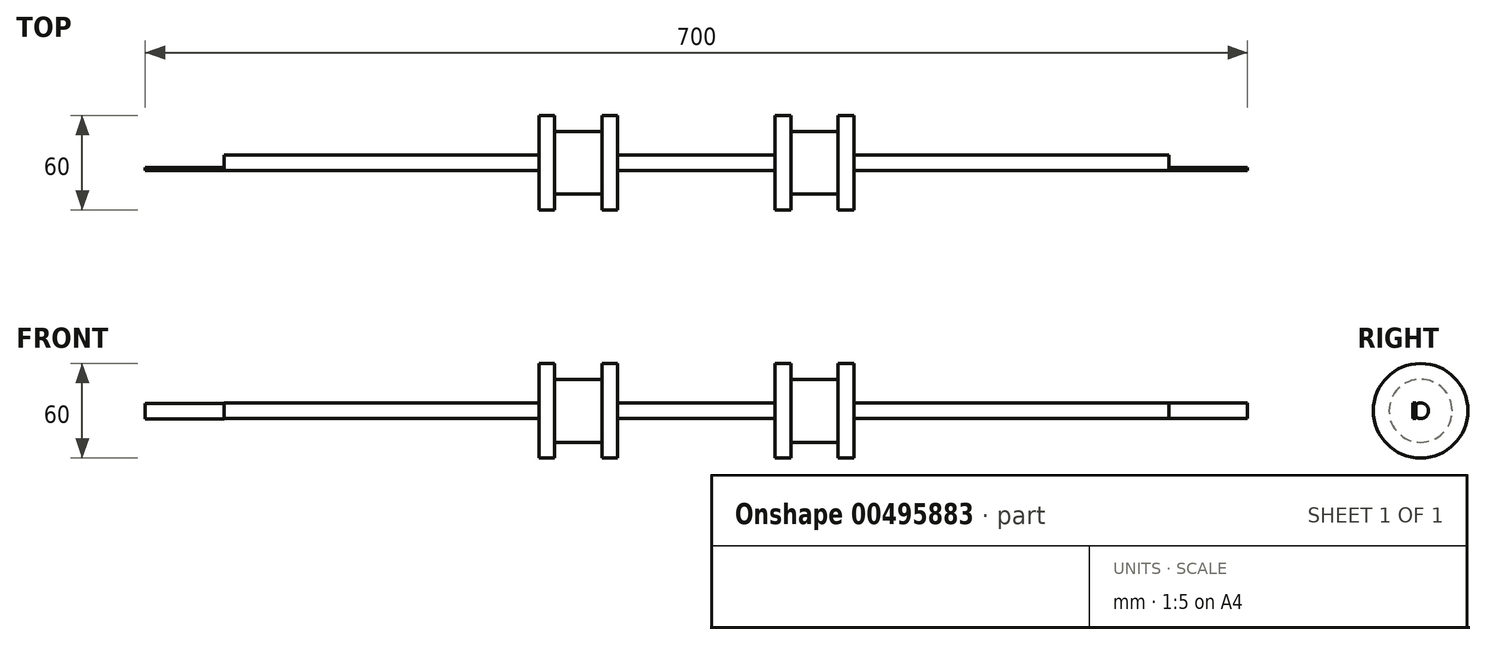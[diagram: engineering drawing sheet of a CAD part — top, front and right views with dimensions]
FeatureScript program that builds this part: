
annotation { "Feature Type Name" : "Feature", "Feature Type Description" : "" }
export const myFeature = defineFeature(function(context is Context, id is Id, definition is map)
    precondition{}
    {
        {
            var Q0;
            Q0=qCreatedBy(makeId("Top.planeOp"),FACE);
            var sketch = newSketch(context, id + "F0", { "sketchPlane" : qUnion([Q0])});
            skLineSegment(sketch, "E0", {"start": v(-300, 0) * mm, "end": v(300, 0) * mm});
            skLineSegment(sketch, "E1", {"start": v(-300, 0) * mm, "end": v(-300, 5) * mm});
            skLineSegment(sketch, "E2", {"start": v(-300, 5) * mm, "end": v(300, 5) * mm});
            skLineSegment(sketch, "E3", {"start": v(300, 5) * mm, "end": v(300, 0) * mm});
            skLineSegment(sketch, "E4", {"start": v(-100, 0) * mm, "end": v(-100, -25) * mm});
            skLineSegment(sketch, "E5", {"start": v(-100, -25) * mm, "end": v(-90, -25) * mm});
            skLineSegment(sketch, "E6", {"start": v(-90, -25) * mm, "end": v(-90, -15) * mm});
            skLineSegment(sketch, "E7", {"start": v(-90, -15) * mm, "end": v(-60, -15) * mm});
            skLineSegment(sketch, "E8", {"start": v(-60, -15) * mm, "end": v(-60, -25) * mm});
            skLineSegment(sketch, "E9", {"start": v(-60, -25) * mm, "end": v(-50, -25) * mm});
            skLineSegment(sketch, "E10", {"start": v(-50, -25) * mm, "end": v(-50, 0) * mm});
            skLineSegment(sketch, "E11", {"start": v(50, 0) * mm, "end": v(50, -25) * mm});
            skLineSegment(sketch, "E12", {"start": v(50, -25) * mm, "end": v(60, -25) * mm});
            skLineSegment(sketch, "E13", {"start": v(60, -25) * mm, "end": v(60, -15) * mm});
            skLineSegment(sketch, "E14", {"start": v(60, -15) * mm, "end": v(90, -15) * mm});
            skLineSegment(sketch, "E15", {"start": v(90, -15) * mm, "end": v(90, -25) * mm});
            skLineSegment(sketch, "E16", {"start": v(90, -25) * mm, "end": v(100, -25) * mm});
            skLineSegment(sketch, "E17", {"start": v(100, -25) * mm, "end": v(100, 0) * mm});
            skSolve(sketch);
        }
        {
            var Q0;
            {var subQ5=sQuery(id+"F0.wireOp",EDGE,"E1");Q0=makeQuery(id+"F0.imprint","IMPRINT",FACE,{"disambiguationData":[TD([[makeQuery(id+"F0.imprint","IMPRINT",EDGE,{"derivedFrom":subQ5}),-1.0]])]});}
            var Q1;
            {var subQ0=sQuery(id+"F0.wireOp",EDGE,"E4");Q1=makeQuery(id+"F0.imprint","IMPRINT",FACE,{"disambiguationData":[TD([[makeQuery(id+"F0.imprint","IMPRINT",EDGE,{"derivedFrom":subQ0}),1.0]])]});}
            var Q2;
            {var subQ0=sQuery(id+"F0.wireOp",EDGE,"E11");Q2=makeQuery(id+"F0.imprint","IMPRINT",FACE,{"disambiguationData":[TD([[makeQuery(id+"F0.imprint","IMPRINT",EDGE,{"derivedFrom":subQ0}),1.0]])]});}
            var Q3;
            Q3=sQuery(id+"F0.wireOp",EDGE,"E2");
            revolve(context, id + "F1", {"entities" : qUnion([Q0, Q1, Q2]), "axis" : qUnion([Q3]), "revolveType" : RevolveType.FULL});
        }
        {
            var Q0;
            Q0=makeQuery(id+"F1.opRevolve","SWEPT_FACE",FACE,{"disambiguationData":[OSD([sQuery(id+"F0.wireOp",EDGE,"E1")])]});
            var sketch = newSketch(context, id + "F2", { "sketchPlane" : qUnion([Q0])});
            skLineSegment(sketch, "E18.bottom", {"start": v(-2, 4.74) * mm, "end": v(0, 4.74) * mm});
            skLineSegment(sketch, "E18.top", {"start": v(-2, -5.26) * mm, "end": v(0, -5.26) * mm});
            skLineSegment(sketch, "E18.left", {"start": v(-2, 4.74) * mm, "end": v(-2, -5.26) * mm});
            skLineSegment(sketch, "E18.right", {"start": v(0, 4.74) * mm, "end": v(0, -5.26) * mm});
            skSolve(sketch);
        }
        {
            var Q0;
            {var subQ0=sQuery(id+"F2.wireOp",EDGE,"E18.top");Q0=makeQuery(id+"F2.imprint","IMPRINT",FACE,{"disambiguationData":[TD([[makeQuery(id+"F2.imprint","IMPRINT",EDGE,{"derivedFrom":subQ0}),1.0]])]});}
            var Q1;
            {var subQ0=sQuery(id+"F2.wireOp",EDGE,"E18.left");var subQ1=makeQuery(id+"F1.opRevolve","SWEPT_EDGE",EDGE,{"disambiguationData":[OSD([sQuery(id+"F0.wireOp",EDGE,"E0"),sQuery(id+"F0.wireOp",EDGE,"E1")])]});var subQ2=makeQuery(id+"F2.imprint","INTERSECT",VERTEX,{"disambiguationData":[OD(0.0)],"derivedFrom":[subQ1,subQ0]});Q1=makeQuery(id+"F2.imprint","IMPRINT",FACE,{"disambiguationData":[TD([[makeQuery(id+"F2.imprint","IMPRINT",EDGE,{"disambiguationData":[TD([[subQ2,-1.0]])],"derivedFrom":subQ0}),1.0]])]});}
            var Q2;
            {var subQ0=sQuery(id+"F2.wireOp",EDGE,"E18.bottom");Q2=makeQuery(id+"F2.imprint","IMPRINT",FACE,{"disambiguationData":[TD([[makeQuery(id+"F2.imprint","IMPRINT",EDGE,{"derivedFrom":subQ0}),-1.0]])]});}
            extrude(context, id + "F3", {"entities" : qUnion([Q0, Q1, Q2]), "operationType" : NewBodyOperationType.ADD, "depth" : 50 * mm});
        }
        {
            var Q0;
            Q0=makeQuery(id+"F1.opRevolve","SWEPT_FACE",FACE,{"disambiguationData":[OSD([sQuery(id+"F0.wireOp",EDGE,"E3")])]});
            var sketch = newSketch(context, id + "F4", { "sketchPlane" : qUnion([Q0])});
            skLineSegment(sketch, "E19.bottom", {"start": v(0, 5) * mm, "end": v(2, 5) * mm});
            skLineSegment(sketch, "E19.top", {"start": v(0, -5) * mm, "end": v(2, -5) * mm});
            skLineSegment(sketch, "E19.left", {"start": v(0, 5) * mm, "end": v(0, -5) * mm});
            skLineSegment(sketch, "E19.right", {"start": v(2, 5) * mm, "end": v(2, -5) * mm});
            skSolve(sketch);
        }
        {
            var Q0;
            {var subQ0=sQuery(id+"F4.wireOp",EDGE,"E19.top");Q0=makeQuery(id+"F4.imprint","IMPRINT",FACE,{"disambiguationData":[TD([[makeQuery(id+"F4.imprint","IMPRINT",EDGE,{"derivedFrom":subQ0}),1.0]])]});}
            var Q1;
            {var subQ0=sQuery(id+"F4.wireOp",EDGE,"E19.bottom");Q1=makeQuery(id+"F4.imprint","IMPRINT",FACE,{"disambiguationData":[TD([[makeQuery(id+"F4.imprint","IMPRINT",EDGE,{"derivedFrom":subQ0}),-1.0]])]});}
            var Q2;
            {var subQ0=sQuery(id+"F4.wireOp",EDGE,"E19.right");var subQ1=makeQuery(id+"F1.opRevolve","SWEPT_EDGE",EDGE,{"disambiguationData":[OSD([sQuery(id+"F0.wireOp",EDGE,"E0"),sQuery(id+"F0.wireOp",EDGE,"E3")])]});var subQ2=makeQuery(id+"F4.imprint","INTERSECT",VERTEX,{"disambiguationData":[OD(0.0)],"derivedFrom":[subQ1,subQ0]});Q2=makeQuery(id+"F4.imprint","IMPRINT",FACE,{"disambiguationData":[TD([[makeQuery(id+"F4.imprint","IMPRINT",EDGE,{"disambiguationData":[TD([[subQ2,-1.0]])],"derivedFrom":subQ0}),-1.0]])]});}
            extrude(context, id + "F5", {"entities" : qUnion([Q0, Q1, Q2]), "operationType" : NewBodyOperationType.ADD, "depth" : 50 * mm});
        }
    });
